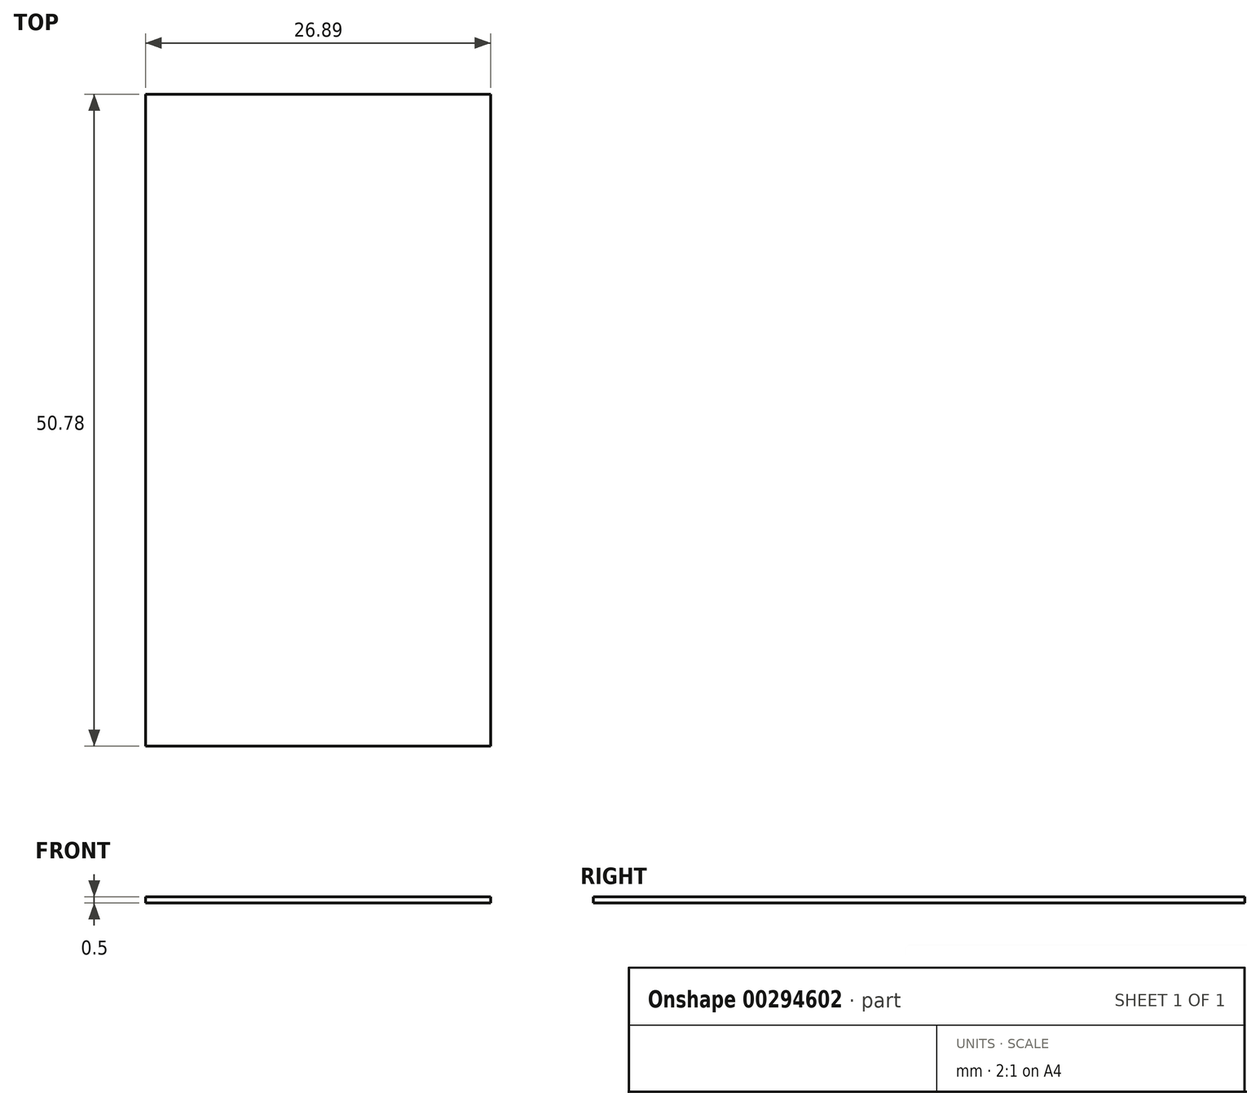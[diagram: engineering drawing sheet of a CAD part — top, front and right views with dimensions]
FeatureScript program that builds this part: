
annotation { "Feature Type Name" : "Feature", "Feature Type Description" : "" }
export const myFeature = defineFeature(function(context is Context, id is Id, definition is map)
    precondition{}
    {
        {
            var Q0;
            Q0=qCreatedBy(makeId("Top.planeOp"),FACE);
            var sketch = newSketch(context, id + "F0", { "sketchPlane" : qUnion([Q0])});
            skLineSegment(sketch, "E0.bottom", {"start": v(-51.42, 20.72) * mm, "end": v(-24.53, 20.72) * mm});
            skLineSegment(sketch, "E0.top", {"start": v(-51.42, -30.06) * mm, "end": v(-24.53, -30.06) * mm});
            skLineSegment(sketch, "E0.left", {"start": v(-51.42, 20.72) * mm, "end": v(-51.42, -30.06) * mm});
            skLineSegment(sketch, "E0.right", {"start": v(-24.53, 20.72) * mm, "end": v(-24.53, -30.06) * mm});
            skSolve(sketch);
        }
        {
            var Q0;
            Q0=makeQuery(id+"F0.imprint","IMPRINT",FACE,{"disambiguationData":[TD([[makeQuery(id+"F0.imprint","IMPRINT",EDGE,{"derivedFrom":sQuery(id+"F0.wireOp",EDGE,"E0.bottom")}),-1.0]])]});
            extrude(context, id + "F1", {"entities" : qUnion([Q0]), "depth" : 0.5 * mm});
        }
    });
